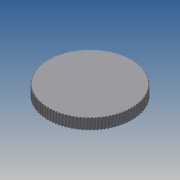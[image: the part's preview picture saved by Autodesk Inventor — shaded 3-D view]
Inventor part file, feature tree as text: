
AUTODESK INVENTOR PART (.ipt)
format: ipt  version: 2013 (Build 170138000, 138)  size: 718,336 bytes
history: native  units: mm
features: extrude x1, pattern_circular x1, sketch x1
ambient origin geometry x8: Origin, YZ Plane, XZ Plane, XY Plane, X Axis, Y Axis, Z Axis, Center Point
bodies: Solid1 (feature_tree)
feature tree (3):
  extrude  "Extrusion1"  Depth=0.628319mm
  pattern_circular  "Circular Pattern1"  [2 undecoded]
  sketch  "Sketch1"  dims[d0=63.661977mm d9=0.628319mm d11=0.254mm d12=0.3mm d13=0.4mm d14=1.0mm d15=0.555mm d16=0.75mm d17=0.254mm d18=8.0mm d19=0.0mm d20=1000.0mm d21=360.0deg d23=0.1mm]
note: 2 required parameter values undecoded (feature->parameter linkage not recoverable at this tier; creation-order binding heuristic only, values carry confidence <= 0.55)
